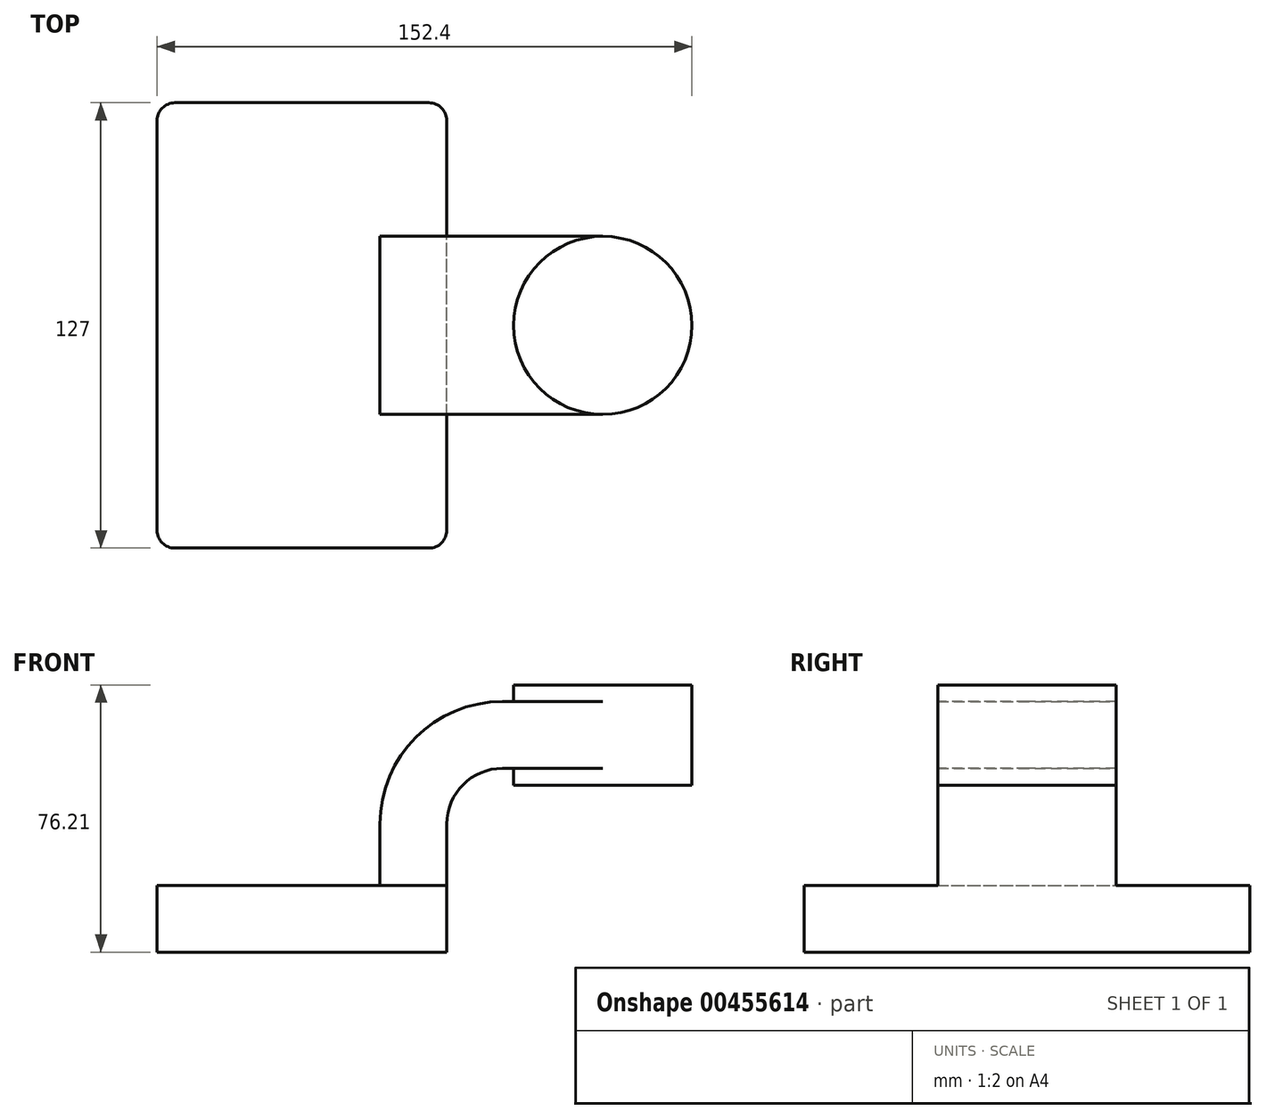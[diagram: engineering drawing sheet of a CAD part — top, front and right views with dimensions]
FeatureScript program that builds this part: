
annotation { "Feature Type Name" : "Feature", "Feature Type Description" : "" }
export const myFeature = defineFeature(function(context is Context, id is Id, definition is map)
    precondition{}
    {
        {
            var Q0;
            Q0=qCreatedBy(makeId("Front.planeOp"),FACE);
            var sketch = newSketch(context, id + "F0", { "sketchPlane" : qUnion([Q0])});
            skLineSegment(sketch, "E0.bottom", {"start": v(41.28, -9.52) * mm, "end": v(-41.27, -9.52) * mm});
            skLineSegment(sketch, "E0.top", {"start": v(41.27, 9.53) * mm, "end": v(-41.28, 9.53) * mm});
            skLineSegment(sketch, "E0.left", {"start": v(41.28, -9.52) * mm, "end": v(41.28, 9.53) * mm});
            skLineSegment(sketch, "E0.right", {"start": v(-41.27, -9.52) * mm, "end": v(-41.28, 9.52) * mm});
            skPoint(sketch, "E0.middle", {"position": v(0, 0) * mm});
            skLineSegment(sketch, "E1.bottom", {"start": v(111.12, 38.1) * mm, "end": v(60.32, 38.1) * mm});
            skLineSegment(sketch, "E1.top", {"start": v(111.12, 66.68) * mm, "end": v(60.32, 66.68) * mm});
            skLineSegment(sketch, "E1.left", {"start": v(111.12, 38.1) * mm, "end": v(111.12, 66.68) * mm});
            skLineSegment(sketch, "E1.right", {"start": v(60.32, 38.1) * mm, "end": v(60.32, 66.68) * mm});
            skPoint(sketch, "E1.middle", {"position": v(85.72, 52.39) * mm});
            skLineSegment(sketch, "E2", {"start": v(41.27, 9.53) * mm, "end": v(41.27, 27) * mm});
            skArc(sketch, "E3", {"start": v(41.27, 27) * mm, "mid": v(45.92, 38.23) * mm, "end": v(57.15, 42.88) * mm});
            skArc(sketch, "E4.1", {"start": v(22.23, 27) * mm, "mid": v(32.45, 51.7) * mm, "end": v(57.15, 61.93) * mm});
            skLineSegment(sketch, "E4.2", {"start": v(22.22, 9.53) * mm, "end": v(22.22, 27) * mm});
            skLineSegment(sketch, "E5", {"start": v(57.15, 42.88) * mm, "end": v(85.72, 42.88) * mm});
            skLineSegment(sketch, "E6", {"start": v(57.15, 61.93) * mm, "end": v(85.72, 61.93) * mm});
            skLineSegment(sketch, "E7", {"start": v(85.72, 38.1) * mm, "end": v(85.72, 66.68) * mm});
            skFitSpline(sketch, "E8", {"points": [v(-41.28, 9.52) * mm, v(57.15, 61.93) * mm], "startDerivative": vector(26.3, 139.17) * mm, "endDerivative": vector(146.6, -3.07) * mm});
            skSolve(sketch);
        }
        {
            var Q0;
            Q0=makeQuery(id+"F0.imprint","IMPRINT",FACE,{"disambiguationData":[TD([[makeQuery(id+"F0.imprint","IMPRINT",EDGE,{"derivedFrom":sQuery(id+"F0.wireOp",EDGE,"E0.bottom")}),-1.0]])]});
            extrude(context, id + "F1", {"entities" : qUnion([Q0]), "endBound" : BoundingType.SYMMETRIC, "depth" : 127 * mm});
        }
        {
            var Q0;
            {var subQ1=sQuery(id+"F0.wireOp",EDGE,"E2");Q0=makeQuery(id+"F0.imprint","IMPRINT",FACE,{"disambiguationData":[TD([[makeQuery(id+"F0.imprint","IMPRINT",EDGE,{"derivedFrom":subQ1}),1.0]])]});}
            var Q1;
            {var subQ0=sQuery(id+"F0.wireOp",EDGE,"E5");var subQ1=sQuery(id+"F0.wireOp",EDGE,"E1.right");var subQ2=makeQuery(id+"F0.imprint","INTERSECT",VERTEX,{"derivedFrom":[subQ1,subQ0]});Q1=makeQuery(id+"F0.imprint","IMPRINT",FACE,{"disambiguationData":[TD([[makeQuery(id+"F0.imprint","IMPRINT",EDGE,{"disambiguationData":[TD([[subQ2,-1.0]])],"derivedFrom":subQ1}),-1.0]])]});}
            extrude(context, id + "F2", {"entities" : qUnion([Q0, Q1]), "operationType" : NewBodyOperationType.ADD, "endBound" : BoundingType.SYMMETRIC, "depth" : 50.8 * mm});
        }
        {
            var Q0;
            Q0=makeQuery(id+"F0.imprint","IMPRINT",FACE,{"disambiguationData":[TD([[makeQuery(id+"F0.imprint","IMPRINT",EDGE,{"derivedFrom":sQuery(id+"F0.wireOp",EDGE,"E4.1")}),1.0]])]});
            extrude(context, id + "F3", {"entities" : qUnion([Q0]), "operationType" : NewBodyOperationType.ADD, "endBound" : BoundingType.SYMMETRIC, "depth" : 15.88 * mm});
        }
        {
            var Q0;
            {var subQ4=sQuery(id+"F0.wireOp",EDGE,"E1.left");Q0=makeQuery(id+"F0.imprint","IMPRINT",FACE,{"disambiguationData":[TD([[makeQuery(id+"F0.imprint","IMPRINT",EDGE,{"derivedFrom":subQ4}),1.0]])]});}
            var Q1;
            Q1=sQuery(id+"F0.wireOp",EDGE,"E7");
            revolve(context, id + "F4", {"operationType" : NewBodyOperationType.ADD, "entities" : qUnion([Q0]), "axis" : qUnion([Q1]), "revolveType" : RevolveType.FULL});
        }
        {
            var Q0;
            Q0=makeQuery(id+"F1.opExtrude","CAP_EDGE",EDGE,{"disambiguationData":[OSD([sQuery(id+"F0.wireOp",EDGE,"E0.right")])],"isStart":false});
            var Q1;
            Q1=makeQuery(id+"F1.opExtrude","CAP_EDGE",EDGE,{"disambiguationData":[OSD([sQuery(id+"F0.wireOp",EDGE,"E0.left")])],"isStart":false});
            var Q2;
            Q2=makeQuery(id+"F1.opExtrude","CAP_EDGE",EDGE,{"disambiguationData":[OSD([sQuery(id+"F0.wireOp",EDGE,"E0.left")])],"isStart":true});
            var Q3;
            Q3=makeQuery(id+"F1.opExtrude","CAP_EDGE",EDGE,{"disambiguationData":[OSD([sQuery(id+"F0.wireOp",EDGE,"E0.right")])],"isStart":true});
            fillet(context, id + "F5", {"entities" : qUnion([Q0, Q1, Q2, Q3]), "radius" : 5.08 * mm, "tangentPropagation" : true, "allowEdgeOverflow" : false});
        }
    });
